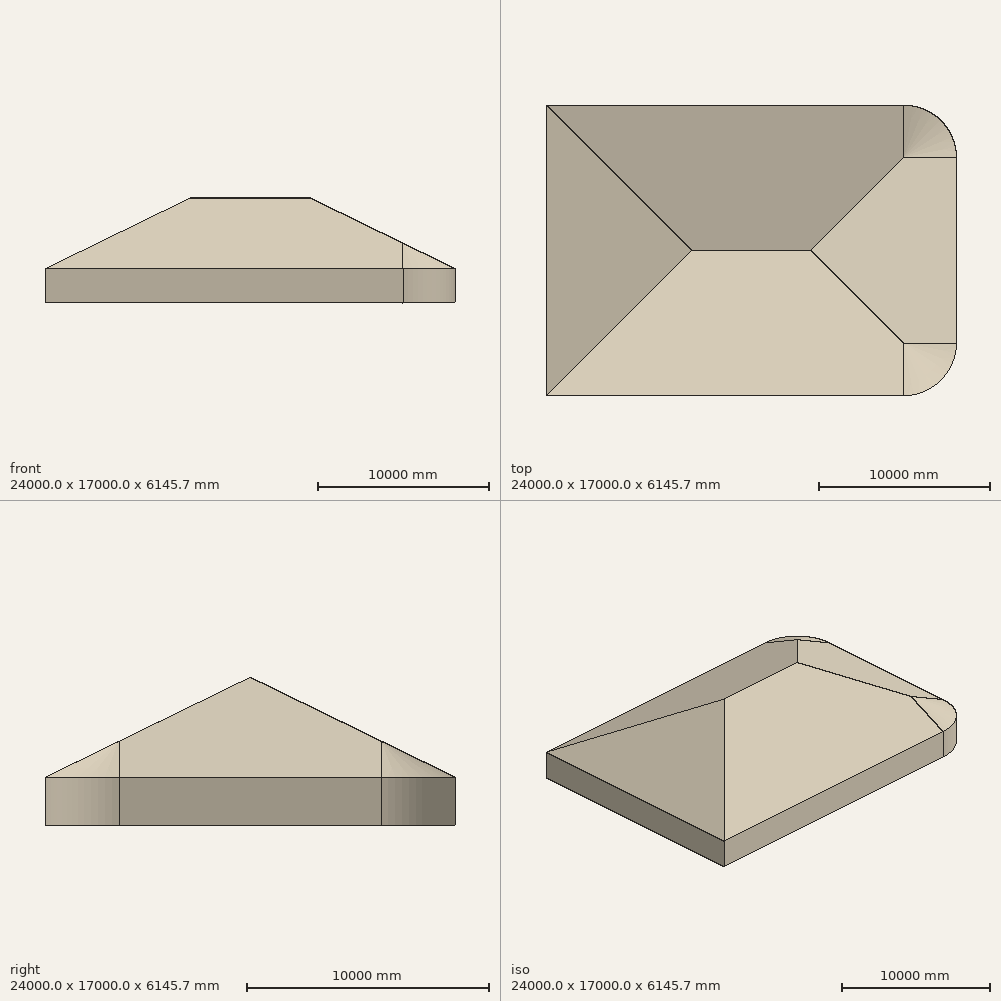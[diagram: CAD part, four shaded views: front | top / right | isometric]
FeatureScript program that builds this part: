
annotation { "Feature Type Name" : "Feature", "Feature Type Description" : "" }
export const myFeature = defineFeature(function(context is Context, id is Id, definition is map)
    precondition{}
    {
        {
            var Q0;
            Q0=qCreatedBy(makeId("Top.planeOp"),FACE);
            var sketch = newSketch(context, id + "F0", { "sketchPlane" : qUnion([Q0])});
            skLineSegment(sketch, "E0.bottom", {"start": v(-104948.3, 21055.58) * mm, "end": v(-84023.3, 21055.58) * mm});
            skLineSegment(sketch, "E0.top", {"start": v(-104948.3, 4055.58) * mm, "end": v(-84023.3, 4055.58) * mm});
            skLineSegment(sketch, "E0.left", {"start": v(-104948.3, 21055.58) * mm, "end": v(-104948.3, 4055.58) * mm});
            skLineSegment(sketch, "E0.right", {"start": v(-80948.3, 17980.58) * mm, "end": v(-80948.3, 7130.58) * mm});
            skPoint(sketch, "E1.visualSharp", {"position": v(-104948.3, 21055.58) * mm});
            skLineSegment(sketch, "E1.filletArc", {"start": v(-104948.3, 21055.58) * mm, "end": v(-104948.3, 21055.58) * mm});
            skPoint(sketch, "E2.visualSharp", {"position": v(-104948.3, 4055.58) * mm});
            skLineSegment(sketch, "E2.filletArc", {"start": v(-104948.3, 4055.58) * mm, "end": v(-104948.3, 4055.58) * mm});
            skPoint(sketch, "E3.visualSharp", {"position": v(-80948.3, 4055.58) * mm});
            skArc(sketch, "E3.filletArc", {"start": v(-84023.3, 4055.58) * mm, "mid": v(-81848.94, 4956.23) * mm, "end": v(-80948.3, 7130.58) * mm});
            skPoint(sketch, "E4.visualSharp", {"position": v(-80948.3, 21055.58) * mm});
            skArc(sketch, "E4.filletArc", {"start": v(-80948.3, 17980.58) * mm, "mid": v(-81848.94, 20154.93) * mm, "end": v(-84023.3, 21055.58) * mm});
            skSolve(sketch);
        }
        {
            var Q0;
            Q0=makeQuery(id+"F0.imprint","IMPRINT",FACE,{"disambiguationData":[TD([[makeQuery(id+"F0.imprint","IMPRINT",EDGE,{"derivedFrom":sQuery(id+"F0.wireOp",EDGE,"E0.bottom")}),-1.0]])]});
            extrude(context, id + "F1", {"entities" : qUnion([Q0]), "flatOperationType" : FlatOperationType.REMOVE, "offsetDistance" : 25 * mm, "depth" : 5000 * mm, "hasDraft" : true, "draftAngle" : 64 * degree, "draftPullDirection" : true, "domain" : OperationDomain.MODEL});
        }
        {
            var Q0;
            Q0=makeQuery(id+"F1.opExtrude","CAP_FACE",FACE,{"disambiguationData":[OSD([sQuery(id+"F0.wireOp",EDGE,"E0.bottom"),sQuery(id+"F0.wireOp",EDGE,"E0.top"),sQuery(id+"F0.wireOp",EDGE,"E0.left"),sQuery(id+"F0.wireOp",EDGE,"E0.right"),sQuery(id+"F0.wireOp",EDGE,"E1.filletArc"),sQuery(id+"F0.wireOp",EDGE,"E2.filletArc"),sQuery(id+"F0.wireOp",EDGE,"E3.filletArc"),sQuery(id+"F0.wireOp",EDGE,"E4.filletArc")])],"isStart":true});
            extrude(context, id + "F2", {"entities" : qUnion([Q0]), "operationType" : NewBodyOperationType.ADD, "flatOperationType" : FlatOperationType.REMOVE, "offsetDistance" : 25 * mm, "depth" : 2000 * mm, "domain" : OperationDomain.MODEL});
        }
    });
